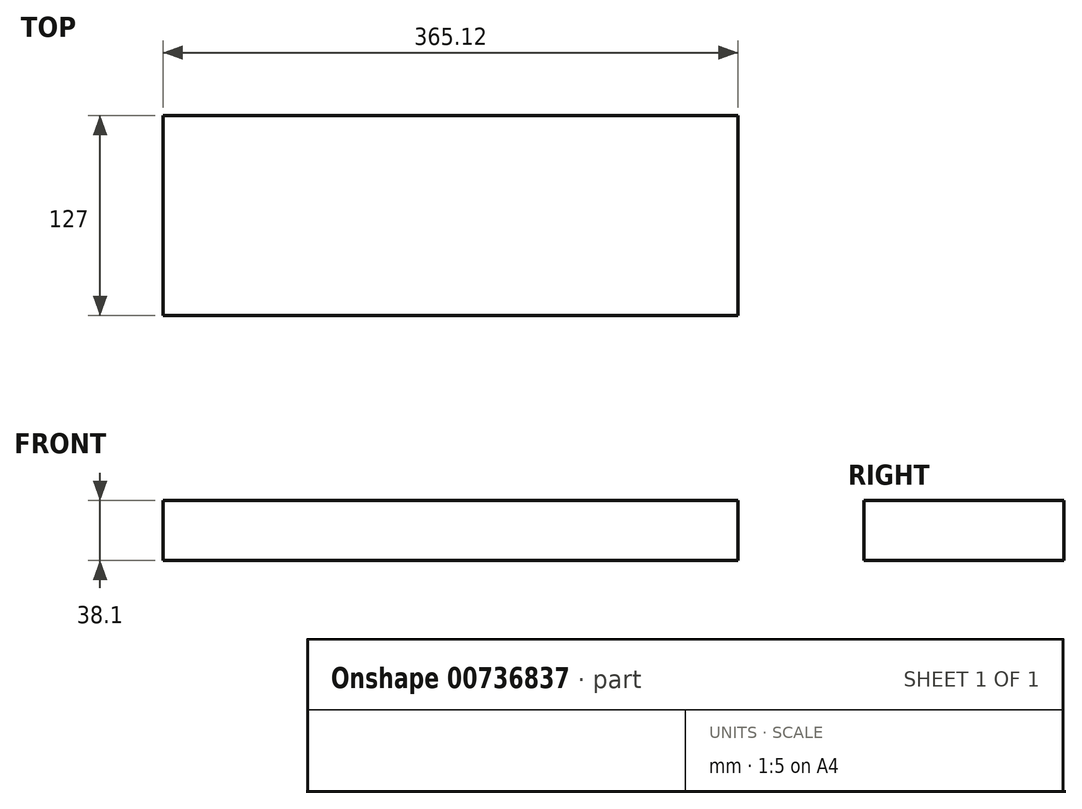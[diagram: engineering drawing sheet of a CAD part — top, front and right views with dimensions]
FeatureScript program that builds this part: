
annotation { "Feature Type Name" : "Feature", "Feature Type Description" : "" }
export const myFeature = defineFeature(function(context is Context, id is Id, definition is map)
    precondition{}
    {
        {
            var Q0;
            Q0=qCreatedBy(makeId("Top.planeOp"),FACE);
            var sketch = newSketch(context, id + "F0", { "sketchPlane" : qUnion([Q0])});
            skLineSegment(sketch, "E0.bottom", {"start": v(-189.54, 55.41) * mm, "end": v(175.58, 55.41) * mm});
            skLineSegment(sketch, "E0.top", {"start": v(-189.54, -71.59) * mm, "end": v(175.58, -71.59) * mm});
            skLineSegment(sketch, "E0.left", {"start": v(-189.54, 55.41) * mm, "end": v(-189.54, -71.59) * mm});
            skLineSegment(sketch, "E0.right", {"start": v(175.58, 55.41) * mm, "end": v(175.58, -71.59) * mm});
            skSolve(sketch);
        }
        {
            var Q0;
            Q0=makeQuery(id+"F0.imprint","IMPRINT",FACE,{"disambiguationData":[TD([[makeQuery(id+"F0.imprint","IMPRINT",EDGE,{"derivedFrom":sQuery(id+"F0.wireOp",EDGE,"E0.bottom")}),-1.0]])]});
            extrude(context, id + "F1", {"entities" : qUnion([Q0]), "depth" : 38.1 * mm, "offsetDistance" : 25.4 * mm});
        }
    });
